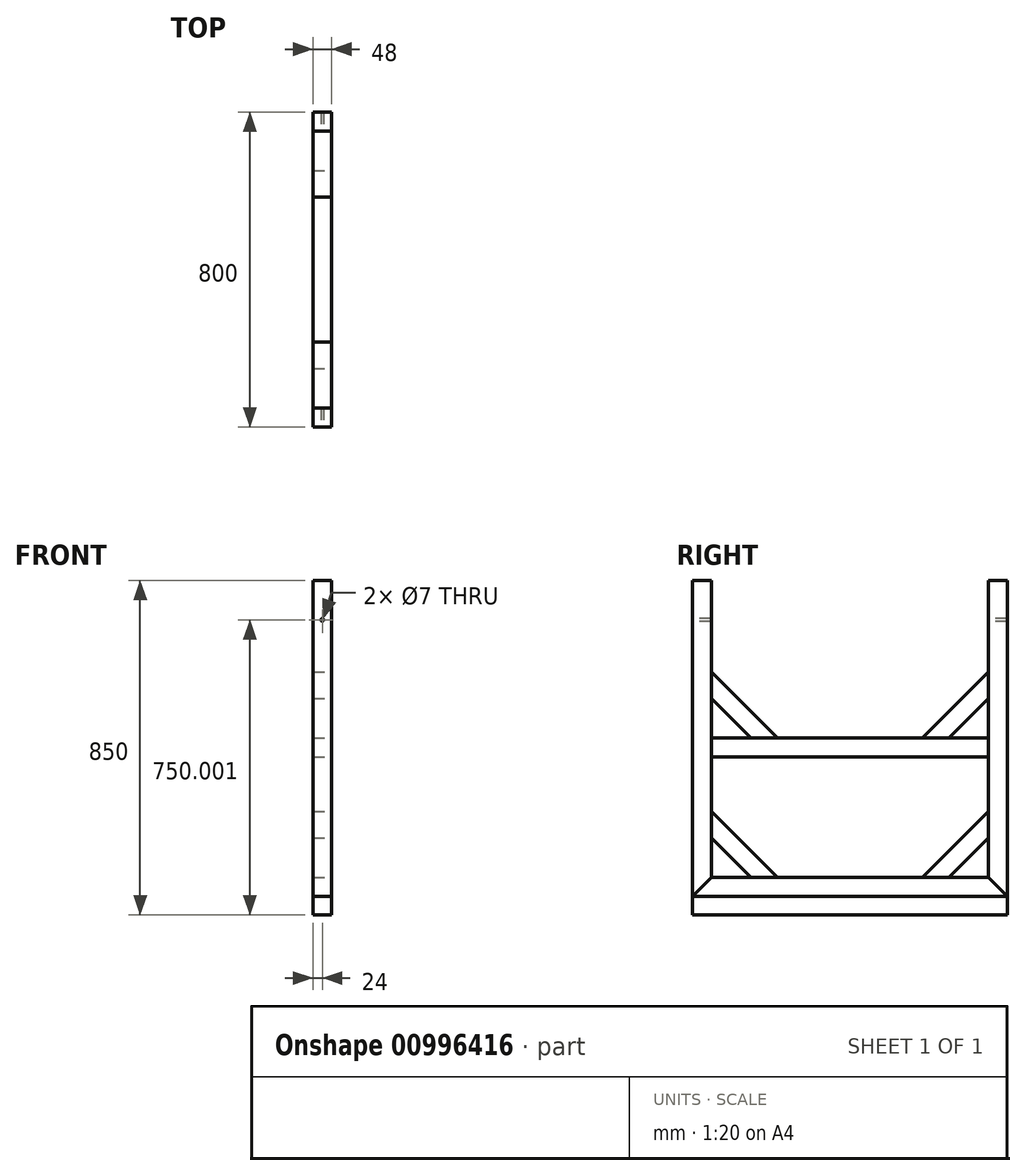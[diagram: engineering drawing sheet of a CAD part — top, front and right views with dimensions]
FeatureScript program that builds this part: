
annotation { "Feature Type Name" : "Feature", "Feature Type Description" : "" }
export const myFeature = defineFeature(function(context is Context, id is Id, definition is map)
    precondition{}
    {
        {
            var Q0;
            Q0=qCreatedBy(makeId("Right.planeOp"),FACE);
            var sketch = newSketch(context, id + "F0", { "sketchPlane" : qUnion([Q0])});
            skLineSegment(sketch, "E0", {"start": v(-214.94, 609.65) * mm, "end": v(-166.94, 609.65) * mm});
            skLineSegment(sketch, "E1", {"start": v(-166.94, 609.65) * mm, "end": v(-166.94, -144.35) * mm});
            skLineSegment(sketch, "E2", {"start": v(-214.94, -240.35) * mm, "end": v(-214.94, 609.65) * mm});
            skLineSegment(sketch, "E3", {"start": v(-166.94, -192.35) * mm, "end": v(537.06, -192.35) * mm});
            skLineSegment(sketch, "E4", {"start": v(585.06, -240.35) * mm, "end": v(-214.94, -240.35) * mm});
            skLineSegment(sketch, "E5", {"start": v(537.06, -144.35) * mm, "end": v(537.06, 609.65) * mm});
            skLineSegment(sketch, "E6", {"start": v(537.06, 609.65) * mm, "end": v(585.06, 609.65) * mm});
            skLineSegment(sketch, "E7", {"start": v(585.06, 609.65) * mm, "end": v(585.06, -240.35) * mm});
            skLineSegment(sketch, "E8", {"start": v(-166.94, 209.65) * mm, "end": v(537.06, 209.65) * mm});
            skLineSegment(sketch, "E9", {"start": v(-166.94, 161.65) * mm, "end": v(537.06, 161.65) * mm});
            skLineSegment(sketch, "E10", {"start": v(-166.94, 309.65) * mm, "end": v(-66.94, 209.65) * mm});
            skLineSegment(sketch, "E11", {"start": v(-166.94, 377.53) * mm, "end": v(0.94, 209.65) * mm});
            skLineSegment(sketch, "E12", {"start": v(537.06, 309.65) * mm, "end": v(437.06, 209.65) * mm});
            skLineSegment(sketch, "E13", {"start": v(537.06, 377.53) * mm, "end": v(369.17, 209.65) * mm});
            skLineSegment(sketch, "E14", {"start": v(537.06, -44.35) * mm, "end": v(437.06, -144.35) * mm});
            skLineSegment(sketch, "E15", {"start": v(537.06, 23.53) * mm, "end": v(369.17, -144.35) * mm});
            skLineSegment(sketch, "E16", {"start": v(-166.94, -44.35) * mm, "end": v(-66.94, -144.35) * mm});
            skLineSegment(sketch, "E17", {"start": v(-166.94, 23.53) * mm, "end": v(0.94, -144.35) * mm});
            skLineSegment(sketch, "E18", {"start": v(-166.94, -144.35) * mm, "end": v(537.06, -144.35) * mm});
            skLineSegment(sketch, "E19", {"start": v(-166.94, -192.35) * mm, "end": v(-214.94, -192.35) * mm});
            skLineSegment(sketch, "E20", {"start": v(-214.94, -192.35) * mm, "end": v(-166.94, -144.35) * mm});
            skLineSegment(sketch, "E21", {"start": v(537.06, -192.35) * mm, "end": v(585.06, -192.35) * mm});
            skLineSegment(sketch, "E22", {"start": v(585.06, -192.35) * mm, "end": v(537.06, -144.35) * mm});
            skSolve(sketch);
        }
        {
            var Q0;
            {var subQ8=sQuery(id+"F0.wireOp",EDGE,"E6");Q0=makeQuery(id+"F0.imprint","IMPRINT",FACE,{"disambiguationData":[TD([[makeQuery(id+"F0.imprint","IMPRINT",EDGE,{"derivedFrom":subQ8}),-1.0]])]});}
            extrude(context, id + "F1", {"entities" : qUnion([Q0]), "oppositeDirection" : true, "depth" : 48 * mm, "offsetDistance" : 25 * mm});
        }
        {
            var Q0;
            {var subQ4=sQuery(id+"F0.wireOp",EDGE,"E0");Q0=makeQuery(id+"F0.imprint","IMPRINT",FACE,{"disambiguationData":[TD([[makeQuery(id+"F0.imprint","IMPRINT",EDGE,{"derivedFrom":subQ4}),-1.0]])]});}
            extrude(context, id + "F2", {"entities" : qUnion([Q0]), "oppositeDirection" : true, "depth" : 48 * mm, "offsetDistance" : 25 * mm});
        }
        {
            var Q0;
            {var subQ0=sQuery(id+"F0.wireOp",EDGE,"E16");Q0=makeQuery(id+"F0.imprint","IMPRINT",FACE,{"disambiguationData":[TD([[makeQuery(id+"F0.imprint","IMPRINT",EDGE,{"derivedFrom":subQ0}),1.0]])]});}
            extrude(context, id + "F3", {"entities" : qUnion([Q0]), "oppositeDirection" : true, "depth" : 48 * mm, "offsetDistance" : 25 * mm});
        }
        {
            var Q0;
            {var subQ0=sQuery(id+"F0.wireOp",EDGE,"E10");Q0=makeQuery(id+"F0.imprint","IMPRINT",FACE,{"disambiguationData":[TD([[makeQuery(id+"F0.imprint","IMPRINT",EDGE,{"derivedFrom":subQ0}),1.0]])]});}
            extrude(context, id + "F4", {"entities" : qUnion([Q0]), "oppositeDirection" : true, "depth" : 48 * mm, "offsetDistance" : 25 * mm});
        }
        {
            var Q0;
            {var subQ0=sQuery(id+"F0.wireOp",EDGE,"E12");Q0=makeQuery(id+"F0.imprint","IMPRINT",FACE,{"disambiguationData":[TD([[makeQuery(id+"F0.imprint","IMPRINT",EDGE,{"derivedFrom":subQ0}),-1.0]])]});}
            extrude(context, id + "F5", {"entities" : qUnion([Q0]), "oppositeDirection" : true, "depth" : 48 * mm, "offsetDistance" : 25 * mm});
        }
        {
            var Q0;
            {var subQ0=sQuery(id+"F0.wireOp",EDGE,"E14");Q0=makeQuery(id+"F0.imprint","IMPRINT",FACE,{"disambiguationData":[TD([[makeQuery(id+"F0.imprint","IMPRINT",EDGE,{"derivedFrom":subQ0}),-1.0]])]});}
            extrude(context, id + "F6", {"entities" : qUnion([Q0]), "oppositeDirection" : true, "depth" : 48 * mm, "offsetDistance" : 25 * mm});
        }
        {
            var Q0;
            {var subQ5=sQuery(id+"F0.wireOp",EDGE,"E9");Q0=makeQuery(id+"F0.imprint","IMPRINT",FACE,{"disambiguationData":[TD([[makeQuery(id+"F0.imprint","IMPRINT",EDGE,{"derivedFrom":subQ5}),1.0]])]});}
            extrude(context, id + "F7", {"entities" : qUnion([Q0]), "oppositeDirection" : true, "depth" : 48 * mm, "offsetDistance" : 25 * mm});
        }
        {
            var Q0;
            Q0=makeQuery(id+"F2.opExtrude","SWEPT_FACE",FACE,{"disambiguationData":[OSD([sQuery(id+"F0.wireOp",EDGE,"E2")])]});
            var sketch = newSketch(context, id + "F8", { "sketchPlane" : qUnion([Q0])});
            skLineSegment(sketch, "E23", {"start": v(-48, 509.65) * mm, "end": v(-24, 509.65) * mm});
            skLineSegment(sketch, "E24", {"start": v(-24, 509.65) * mm, "end": v(0, 509.65) * mm});
            skCircle(sketch, "E25", {"center": v(-24, 509.65) * mm, "radius": 3.5 * mm});
            skPoint(sketch, "E26.orphan", {"position": v(-24, 609.65) * mm});
            skSolve(sketch);
        }
        {
            var Q0;
            Q0=qSketchRegion(id+"F8",true);
            extrude(context, id + "F9", {"entities" : qUnion([Q0]), "operationType" : NewBodyOperationType.REMOVE, "endBound" : BoundingType.THROUGH_ALL, "oppositeDirection" : true, "depth" : 25 * mm, "offsetDistance" : 25 * mm});
        }
        {
            var Q0;
            Q0=makeQuery(id+"F0.imprint","IMPRINT",FACE,{"disambiguationData":[TD([[makeQuery(id+"F0.imprint","IMPRINT",EDGE,{"derivedFrom":sQuery(id+"F0.wireOp",EDGE,"E3")}),1.0]])]});
            extrude(context, id + "F10", {"entities" : qUnion([Q0]), "oppositeDirection" : true, "depth" : 48 * mm, "offsetDistance" : 25 * mm});
        }
        {
            var Q0;
            Q0=makeQuery(id+"F0.imprint","IMPRINT",FACE,{"disambiguationData":[TD([[makeQuery(id+"F0.imprint","IMPRINT",EDGE,{"derivedFrom":sQuery(id+"F0.wireOp",EDGE,"E3")}),-1.0]])]});
            extrude(context, id + "F11", {"entities" : qUnion([Q0]), "oppositeDirection" : true, "depth" : 48 * mm, "offsetDistance" : 25 * mm});
        }
    });
